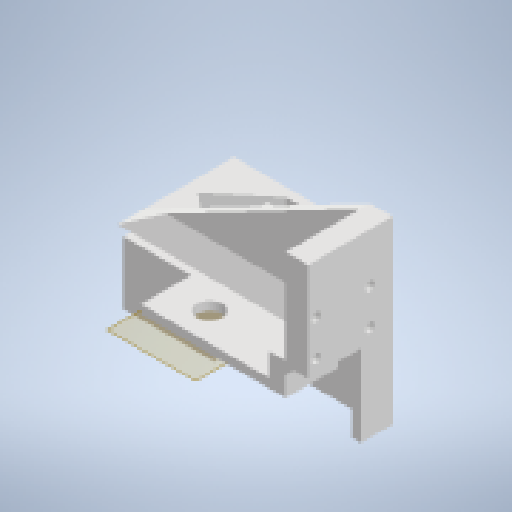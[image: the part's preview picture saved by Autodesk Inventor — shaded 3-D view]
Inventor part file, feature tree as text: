
AUTODESK INVENTOR PART (.ipt)
format: ipt  version: 2024.2 (Build 282272000, 272)  size: 317,952 bytes
history: native  units: mm
features: extrude x14, sketch x12, other x7, reference x6, chamfer x4, projected_geometry x2
ambient origin geometry x8: Origin, YZ Plane, XZ Plane, XY Plane, X Axis, Y Axis, Z Axis, Center Point
bodies: Body1 (feature_tree)
feature tree (45):
  other  "Твердое тело1"
  other  "РабПлоскость1"
  sketch  "Эскиз1"
  extrude  "Выдавливание1"  Depth=2.0mm TaperAngle=0.0deg
  extrude  "Выдавливание2"  Depth=1.5mm
  extrude  "Выдавливание3"  Depth=1.5mm
  extrude  "Выдавливание4"  Depth=12.0mm TaperAngle=0.0deg
  extrude  "Выдавливание5"  Depth=8.0mm TaperAngle=0.0deg
  extrude  "Выдавливание6"  Depth=12.0mm TaperAngle=0.0deg
  extrude  "Выдавливание7"  Depth=20.0mm
  sketch  "Эскиз6"
  extrude  "Выдавливание8"  Depth=18.0mm
  extrude  "Выдавливание9"  Depth=2.0mm
  sketch  "Эскиз7"
  other  "РабПлоскость2"
  extrude  "Выдавливание10"  Depth=18.9mm
  extrude  "Выдавливание11"  Depth=22.9mm
  extrude  "Выдавливание12"  Depth=3.0mm
  sketch  "Эскиз10"
  extrude  "Выдавливание13"  TaperAngle=0.0deg  [1 undecoded]
  extrude  "Выдавливание14"  Depth=4.2mm
  chamfer  "Фаска2"  [1 undecoded]
  chamfer  "Фаска3"  Distance=2.0mm
  chamfer  "Фаска4"  Distance=1.500103mm
  chamfer  "Фаска5"  Distance=19.2mm
  reference  "Ссылка1"
  reference  "Ссылка2"
  reference  "Ссылка3"
  sketch  "Эскиз2"
  sketch  "Эскиз3"
  sketch  "Эскиз4"
  sketch  "Эскиз5"
  reference  "Ссылка4"
  reference  "Ссылка5"
  projected_geometry  "Спроецированная петля1"
  sketch  "Эскиз8"
  sketch  "Эскиз9"
  reference  "Ссылка6"
  projected_geometry  "Спроецированная петля2"
  sketch  "Эскиз11"
  sketch  "Эскиз12"
  other  "<userpath>\Documents\Artist-v2\3D\каретка.iam"
  other  "каретка.iam"
  other  "крепежная основа:1"
  other  "Сервопривод:1"
note: 2 required parameter values undecoded (feature->parameter linkage not recoverable at this tier; creation-order binding heuristic only, values carry confidence <= 0.55)
